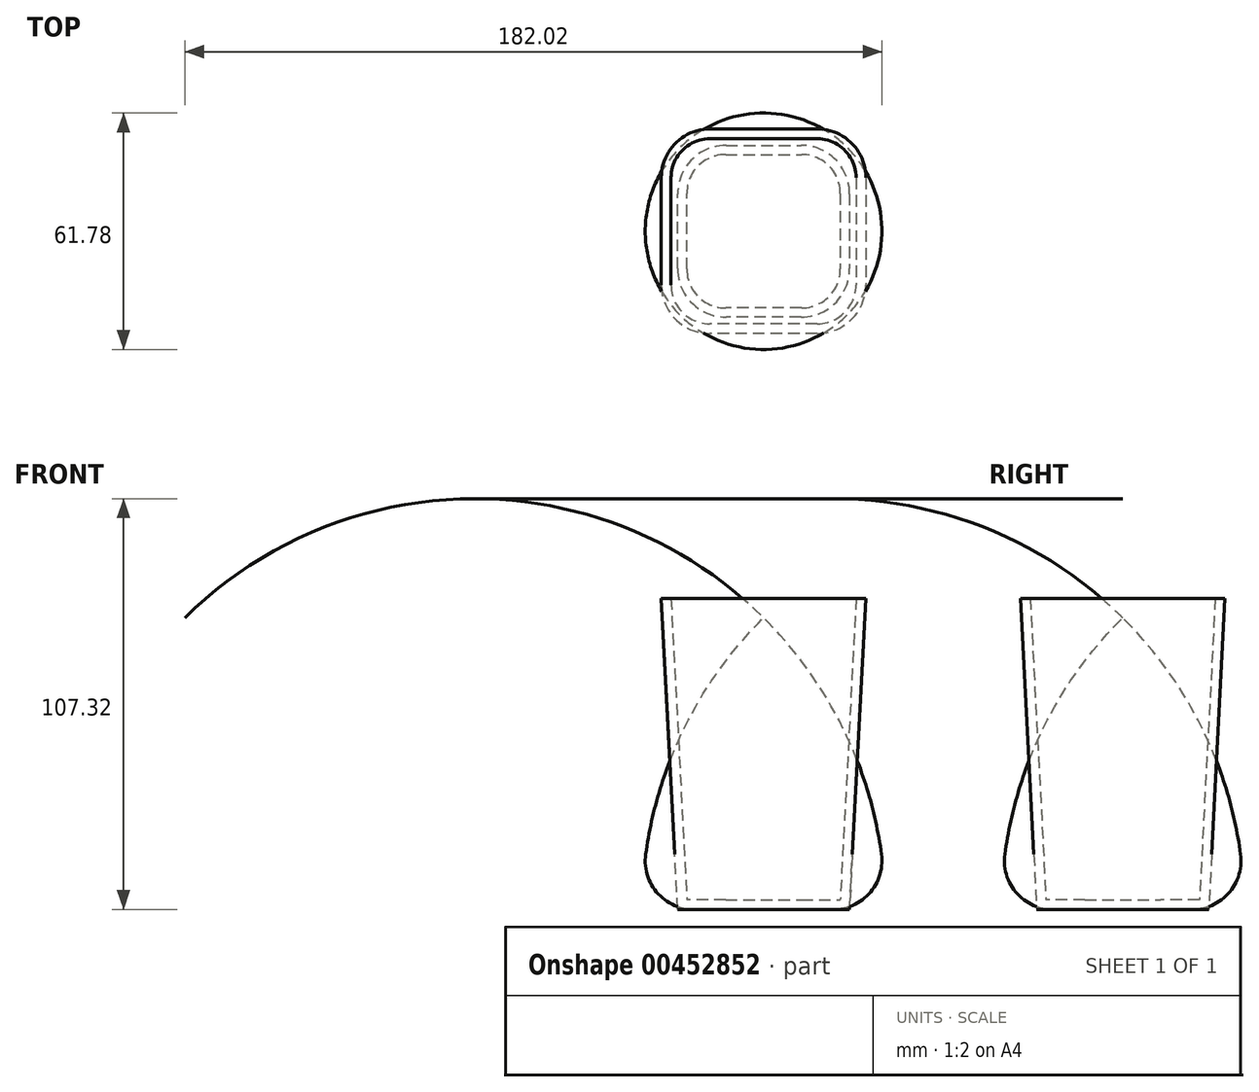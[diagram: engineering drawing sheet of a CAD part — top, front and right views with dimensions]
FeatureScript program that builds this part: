
annotation { "Feature Type Name" : "Feature", "Feature Type Description" : "" }
export const myFeature = defineFeature(function(context is Context, id is Id, definition is map)
    precondition{}
    {
        {
            var Q0;
            Q0=qCreatedBy(makeId("Front.planeOp"),FACE);
            var sketch = newSketch(context, id + "F0", { "sketchPlane" : qUnion([Q0])});
            skLineSegment(sketch, "E0", {"start": v(0, 0) * mm, "end": v(0, 76.2) * mm});
            skArc(sketch, "E1", {"start": v(31.75, 0) * mm, "mid": v(23.5, 41.27) * mm, "end": v(0, 76.2) * mm});
            skLineSegment(sketch, "E2", {"start": v(0, 0) * mm, "end": v(31.75, 0) * mm});
            skSolve(sketch);
        }
        {
            var Q0;
            Q0 = qSketchRegion(id + "F0", true);
            var Q1;
            Q1=sQuery(id+"F0.wireOp",EDGE,"E0");
            revolve(context, id + "F1", {"entities" : qUnion([Q0]), "axis" : qUnion([Q1]), "revolveType" : RevolveType.FULL});
        }
        {
            var Q0;
            Q0=qCreatedBy(makeId("Top.planeOp"),FACE);
            var sketch = newSketch(context, id + "F2", { "sketchPlane" : qUnion([Q0])});
            skLineSegment(sketch, "E3.bottom", {"start": v(-22.45, 22.45) * mm, "end": v(22.45, 22.45) * mm});
            skLineSegment(sketch, "E3.top", {"start": v(-22.45, -22.45) * mm, "end": v(22.45, -22.45) * mm});
            skLineSegment(sketch, "E3.left", {"start": v(-22.45, 22.45) * mm, "end": v(-22.45, -22.45) * mm});
            skLineSegment(sketch, "E3.right", {"start": v(22.45, 22.45) * mm, "end": v(22.45, -22.45) * mm});
            skPoint(sketch, "E3.middle", {"position": v(0, 0) * mm});
            skCircle(sketch, "E4.0", {"center": v(0, 0) * mm, "radius": 31.75 * mm, "construction": true});
            skLineSegment(sketch, "E5", {"start": v(-22.45, 0) * mm, "end": v(22.45, 0) * mm, "construction": true});
            skSolve(sketch);
        }
        {
            var Q0;
            Q0 = qSketchRegion(id + "F2", true);
            extrude(context, id + "F3", {"entities" : qUnion([Q0]), "depth" : 81.28 * mm, "hasDraft" : true, "draftAngle" : 3 * degree});
        }
        {
            var Q0;
            Q0=makeQuery(id+"F3.opExtrude","SWEPT_EDGE",EDGE,{"disambiguationData":[OSD([sQuery(id+"F2.wireOp",EDGE,"E3.top"),sQuery(id+"F2.wireOp",EDGE,"E3.left")])]});
            var Q1;
            Q1=makeQuery(id+"F3.opExtrude","SWEPT_EDGE",EDGE,{"disambiguationData":[OSD([sQuery(id+"F2.wireOp",EDGE,"E3.top"),sQuery(id+"F2.wireOp",EDGE,"E3.right")])]});
            var Q2;
            Q2=makeQuery(id+"F3.opExtrude","SWEPT_EDGE",EDGE,{"disambiguationData":[OSD([sQuery(id+"F2.wireOp",EDGE,"E3.bottom"),sQuery(id+"F2.wireOp",EDGE,"E3.left")])]});
            var Q3;
            Q3=makeQuery(id+"F3.opExtrude","SWEPT_EDGE",EDGE,{"disambiguationData":[OSD([sQuery(id+"F2.wireOp",EDGE,"E3.bottom"),sQuery(id+"F2.wireOp",EDGE,"E3.right")])]});
            fillet(context, id + "F4", {"entities" : qUnion([Q0, Q1, Q2, Q3]), "radius" : 12.7 * mm, "tangentPropagation" : true, "allowEdgeOverflow" : false});
        }
        {
            var Q0;
            Q0=makeQuery(id+"F1.opRevolve","SWEPT_EDGE",EDGE,{"disambiguationData":[OSD([sQuery(id+"F0.wireOp",EDGE,"E1"),sQuery(id+"F0.wireOp",EDGE,"E2")])]});
            fillet(context, id + "F5", {"entities" : qUnion([Q0]), "radius" : 12.7 * mm, "tangentPropagation" : true, "allowEdgeOverflow" : false});
        }
        {
            var Q0;
            Q0=makeQuery(id+"F3.opExtrude","CAP_FACE",FACE,{"disambiguationData":[OSD([sQuery(id+"F2.wireOp",EDGE,"E3.bottom"),sQuery(id+"F2.wireOp",EDGE,"E3.top"),sQuery(id+"F2.wireOp",EDGE,"E3.left"),sQuery(id+"F2.wireOp",EDGE,"E3.right")])],"isStart":false});
            shell(context, id + "F6", {"entities" : qUnion([Q0]), "thickness" : 2.54 * mm});
        }
    });
